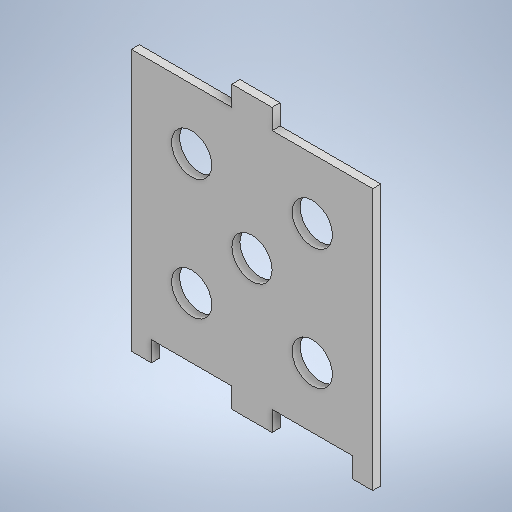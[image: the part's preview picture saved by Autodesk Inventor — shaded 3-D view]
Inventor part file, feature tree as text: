
AUTODESK INVENTOR PART (.ipt)
format: ipt  version: 2025.1 (Build 291241020, 241B)  size: 283,648 bytes
history: native  units: in
note: dims shown in document units (in); Inventor stores cm internally (conversion verified against a paired STEP export)
features: extrude x2, sketch x2
ambient origin geometry x8: Origin, YZ Plane, XZ Plane, XY Plane, X Axis, Y Axis, Z Axis, Center Point
bodies: Solid1 (feature_tree)
feature tree (4):
  extrude  "Extrusion1"  Depth=6.0in
  extrude  "Extrusion2"  Depth=0.5in
  sketch  "Sketch1"  dims[d0=6.0in d1=6.0in]
  sketch  "Sketch2"  dims[d5=0.5in d6=0.5in d7=0.5in d8=0.5in d9=2.5in d10=90.0deg d11=1.0in d12=1.0in d13=1.0in d14=1.0in d15=1.0in d16=1.5in d17=1.5in d18=1.5in d19=1.5in d20=3.0in d21=3.0in d22=1.5in d23=1.5in d24=1.5in d25=1.5in d26=0.5in d27=0.2in d28=0.0in d29=0.5in d31=0.5in d32=0.5in d33=0.0in]
